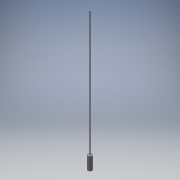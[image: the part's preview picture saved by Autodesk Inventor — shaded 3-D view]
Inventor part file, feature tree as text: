
AUTODESK INVENTOR PART (.ipt)
format: ipt  version: 2016 (Build 200138000, 138)  size: 92,672 bytes
history: native  units: in
note: dims shown in document units (in); Inventor stores cm internally (conversion verified against a paired STEP export)
features: sketch x3, extrude x2
ambient origin geometry x8: Origin, YZ Plane, XZ Plane, XY Plane, X Axis, Y Axis, Z Axis, Center Point
bodies: Solid1 (feature_tree)
feature tree (5):
  extrude  "Extrusion1"  Depth=3.0in TaperAngle=0.0deg
  extrude  "Extrusion2"  Depth=29.0in TaperAngle=0.0deg
  sketch  "Sketch3"
  sketch  "Sketch1"  dims[d0=1.0in d1=3.0in d2=0.0in]
  sketch  "Sketch2"  dims[d3=0.25in d4=29.0in d5=0.0in]
